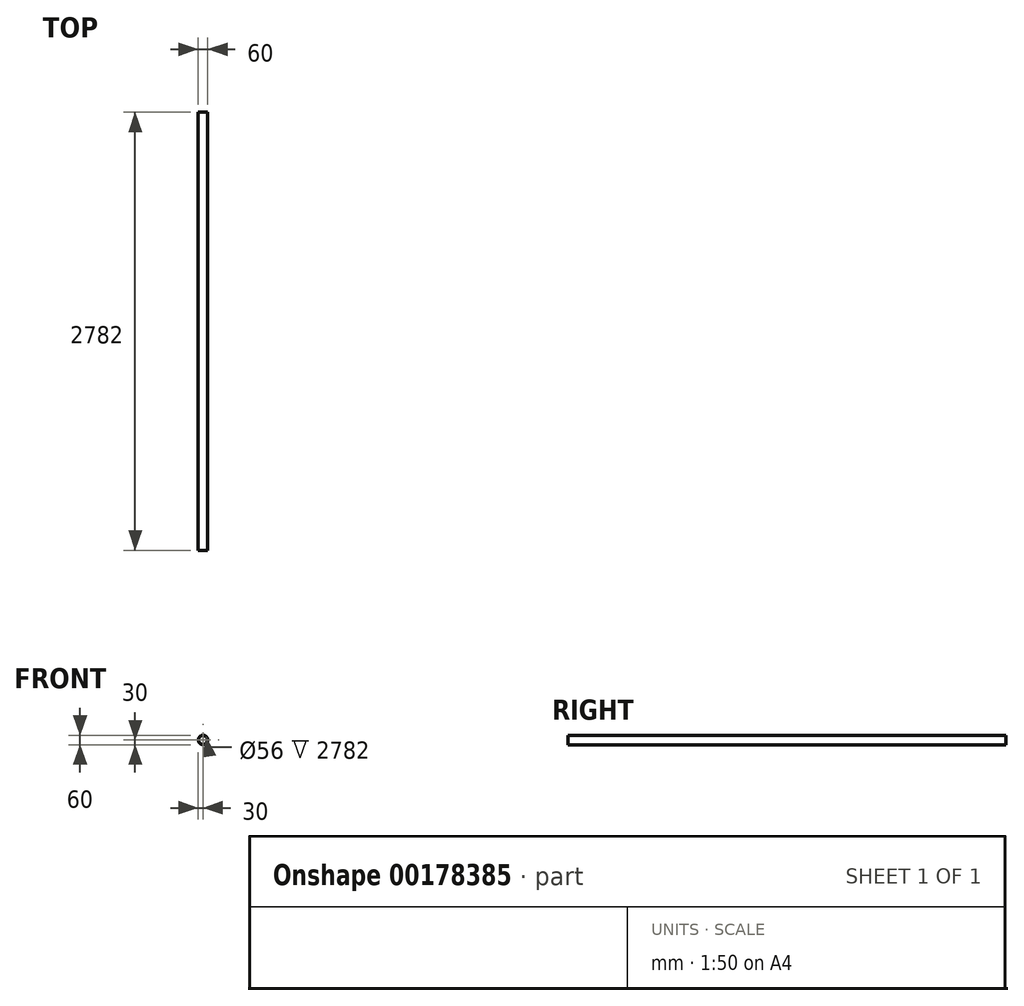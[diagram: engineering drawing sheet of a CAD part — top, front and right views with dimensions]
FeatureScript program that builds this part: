
annotation { "Feature Type Name" : "Feature", "Feature Type Description" : "" }
export const myFeature = defineFeature(function(context is Context, id is Id, definition is map)
    precondition{}
    {
        {
            var Q0;
            Q0=qCreatedBy(makeId("Front.planeOp"),FACE);
            var sketch = newSketch(context, id + "F0", { "sketchPlane" : qUnion([Q0])});
            skCircle(sketch, "E0", {"center": v(0, 0) * mm, "radius": 30 * mm});
            skCircle(sketch, "E1.0", {"center": v(0, 0) * mm, "radius": 28 * mm});
            skSolve(sketch);
        }
        {
            var Q0;
            Q0=makeQuery(id+"F0.imprint","IMPRINT",FACE,{"disambiguationData":[TD([[makeQuery(id+"F0.imprint","IMPRINT",EDGE,{"derivedFrom":sQuery(id+"F0.wireOp",EDGE,"E0")}),1.0]])]});
            extrude(context, id + "F1", {"entities" : qUnion([Q0]), "depth" : 2782 * mm});
        }
    });
